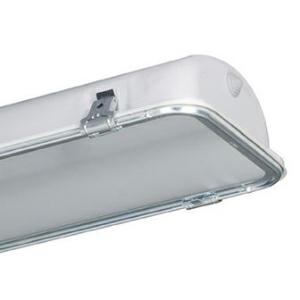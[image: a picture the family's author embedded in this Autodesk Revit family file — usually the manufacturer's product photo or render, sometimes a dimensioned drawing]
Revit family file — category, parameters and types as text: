
# Revit family: 3f_filippi_-_beta_i3f_76_vs_ampio_3f_filippi_-_55138_-_i3f_led_762x30w_ampio_vs_l1565
name_source: partatom
category: Lighting Fixtures
units: mm (PartAtom-declared; Revit-internal decimal feet)

## family parameters
Cut with Voids When Loaded = No
Host = Face
Light Source = No
Part Type = Normal
Room Calculation Point = No
Round Connector Dimension = Use Diameter
Shared = No

## types (1)
- 3F Filippi - Beta i3F 76 VS Ampio (1 x LED, 8820 lm, 66 W, 4000 K)
    Apparent Load = 66 VA
    Approval mark = ENEC
    CIE Flux Codes = 62 90 98 100 100
    Color Rendering = 80
    Color Temperature = 4000 K
    Control Gear = Electronic ballast
    Default Elevation = 1800 mm
    Description = ILLUMINOTECHNICAL
Luminous efficiency 100% (DLOR 100%, ULOR 0%).
Initial luminous flux of the luminaire 8820 lm.
Wide symmetric distribution.
Installation Interdistance Transv.D = 1.31 x hu - Long.D = 1.31 x hu.
Tabular UGR (CIE 117 - 4H-8H; S=0.25H; 70/50/20): RUG 19.8 - 21.1.
Beam angle: 90° - 99°.
Luminous efficacy 134 lm/W.
Lifetime (L93/B10): 30000 h. (tq+25°C)
Lifetime (L90/B10): 50000 h. (tq+25°C)
Lifetime (L85/B10): 80000 h. (tq+25°C)
Lifetime (L80/B10): 100000 h. (tq+25°C)
Lifetime (L85/B10): 50000 h. (tq+35°C)
Sudden decreased luminous flux after 50000 hours: 0% (C0).
Photobiological safety in compliance with IEC/TR 62778: RG0 risk exempt, (IEC 62471).
In compliance with IEC/EN 62722-2-1 - IEC/EN 62717 standards.

SOURCE
2 linear LED modules 30W/840.
Energy efficiency class (UE 2019/2020 - UE 2019/2015): D.
CIE 13.3 Colour rendering index: CRI >80 (R9 <50%).
IES TM-30 Fidelity Index: Rf = 84 Rg = 95.
CCT nominal colour temperature 4000 K.
Colour initial tolerance (MacAdam): SDCM 3.

MECHANICAL
Single-piece housing in pressed steel, powder-coated in white epoxy-polyester.
Moulded anti-glare glass, non-combustible, tempered, mounted and locked to the single-piece galvanised steel perimetrical frame, sealing gasket, hinged opening by means of galvanised steel clips.
Wide flow recuperator, oversized, in specular aluminium with superficial titanium-magnesium treatment, non-iridescent.
Gear-tray unit in hot-galvanised steel, painted in white polyester, fixed to the housing by means of "Ribloc" rapid devices in galvanised steel, hinged opening.
Luminaire with limited surface temperature. - D - (EN 60598-2-24)
Dimensions: 1565x235 mm, height 105 mm. Weight 9.75 kg.
IP65 protection degree.
Mechanical strength to impacts IK09 (10 joule).
Glow-wire test resistance 960°C.

ELECTRICAL
Halogen Free electronic wiring 230V-50/60Hz, power factor 0.97, THD <25%, constant output current, SELV, class I, 1 driver.
Power of the luminaire 66 W.
CE - IEC 60598-1 - EN 60598-1.
SAFE FLICKER: PstLM=<1 and SVM=<0.4 (IEC TR 61547-1 and IEC TR 63158), to ensure a more comfortable and safe light.
Luminaire compliant with EN 60598-2-22 for power supply from a centralised emergency system CPSS (Central Power Supply System), not incorporated in the luminaire - high risk areas excluded. The default power and flux are 100% in AC and 100% in DC.
Ambient temperature from -20°C to +35°C.
Temperature class T6 max 85°C.
Relative humidity UR: <85%.

INSTALLATION
Ceiling / Suspended / Wall.
All accessories dedicated to this product are available on the Catalog and on our website www.3F-Filippi.com.

APPLICATIONS
In industrial environments, stores and dry, dusty indoor environments, subject to occasional water splashes.

WARNING
Fixture not suitable for cold stores with an ambient temperature <0°C and/or relative humidity >85%.
Luminaire designed for disposal/recycling at end-of-life.
Replaceable (LED only) light source by a professional. Replaceable control gear by a professional.
    Height = 105 mm
    Lamp = 1 x LED
    Lamp Light Flux = 8820 lm
    Lamp Power = 66 W
    Lamp count = 1
    Length = 1565 mm
    Lifetime = 50000 h
    Luminous efficacy = 134 lm/W
    Manufacturer = 3F Filippi
    ModVariant = No
    Model = 3F Filippi - 55138 - i3F LED 762x30W AMPIO VS L1565
    Mounting Place = Ceiling
    Mounting Type = Pendant
    Number of Poles = 1
    OnlyDefault = Yes
    Power Factor = 1
    Product Name = 3F Filippi - Beta i3F 76 VS Ampio
    Product group = pendant luminaire
    ProductGroupID = 9
    Protection Class = Protection class I
    Protection Degree = IP 65
    RLX_Detail_Level = 1
    RLX_Emergency_Light_Flux = 0 lm
    RLX_Emergency_Type = 0
    RLX_Emergency_Type_DB = No
    RlxData = <blob elided: 64349 chars, md5=c9191774>
    Socket = socket
    Standby Power = 0 W
    System Light Flux = 8820 lm
    System Power = 66 W
    Type Comments = Product without accessories
    Type Image = 3ffilippi_55138.jpg
    URL = http://relux.com
    VarID = ---
    Voltage = 0 V
    Weight = 0.00 kg
    Width = 235 mm

## geometry (parser evidence)
native form markers: Blend x4, Sweep x10
no freeform markers — native parametric forms only
